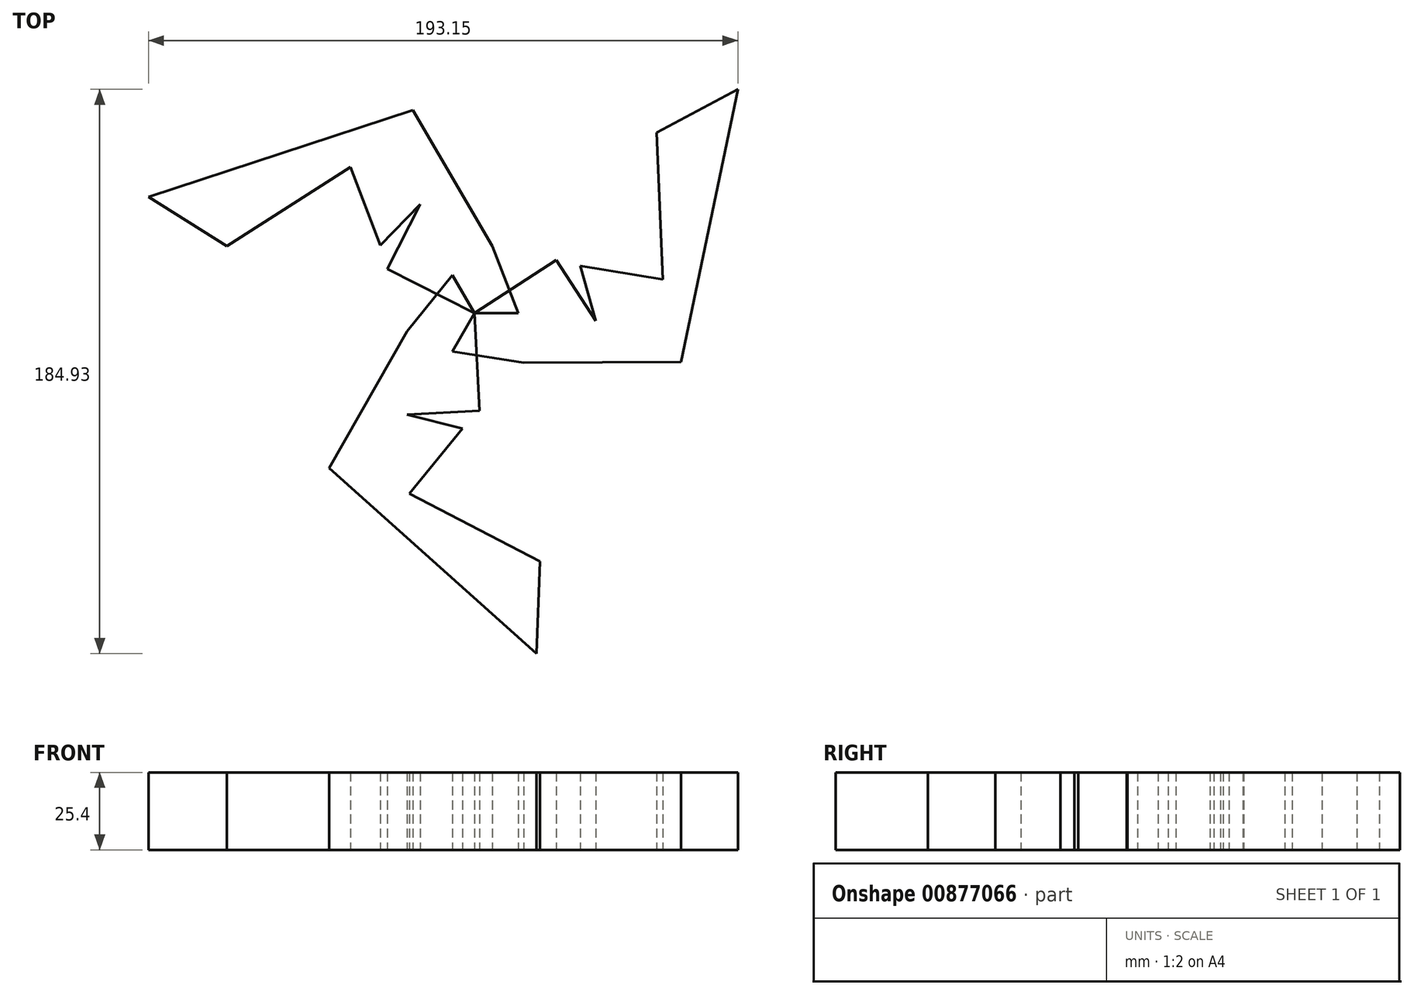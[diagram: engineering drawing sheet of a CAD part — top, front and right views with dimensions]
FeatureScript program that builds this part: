
annotation { "Feature Type Name" : "Feature", "Feature Type Description" : "" }
export const myFeature = defineFeature(function(context is Context, id is Id, definition is map)
    precondition{}
    {
        {
            var Q0;
            Q0=qCreatedBy(makeId("Top.planeOp"),FACE);
            var sketch = newSketch(context, id + "F0", { "sketchPlane" : qUnion([Q0])});
            skLineSegment(sketch, "E0", {"start": v(0, 0) * mm, "end": v(-28.53, 14.58) * mm});
            skLineSegment(sketch, "E1", {"start": v(-28.53, 14.58) * mm, "end": v(-17.72, 35.74) * mm});
            skLineSegment(sketch, "E2", {"start": v(-17.72, 35.74) * mm, "end": v(-30.77, 22.27) * mm});
            skLineSegment(sketch, "E3", {"start": v(-30.77, 22.27) * mm, "end": v(-40.57, 47.95) * mm});
            skLineSegment(sketch, "E4", {"start": v(-40.57, 47.95) * mm, "end": v(-81.18, 22.03) * mm});
            skLineSegment(sketch, "E5", {"start": v(-81.18, 22.03) * mm, "end": v(-106.77, 38.1) * mm});
            skLineSegment(sketch, "E6", {"start": v(-106.77, 38.1) * mm, "end": v(-20.11, 66.62) * mm});
            skLineSegment(sketch, "E7", {"start": v(-20.11, 66.62) * mm, "end": v(5.94, 22.03) * mm});
            skLineSegment(sketch, "E8", {"start": v(5.94, 22.03) * mm, "end": v(14.45, 0) * mm});
            skLineSegment(sketch, "E9", {"start": v(14.45, 0) * mm, "end": v(0, 0) * mm});
            skSolve(sketch);
        }
        {
            var Q0;
            Q0 = qSketchRegion(id + "F0", true);
            extrude(context, id + "F1", {"entities" : qUnion([Q0]), "depth" : 25.4 * mm, "offsetDistance" : 25.4 * mm});
        }
        {
            var Q0;
            Q0=makeQuery(id+"F1.opExtrude","SWEPT_BODY",BODY,{"disambiguationData":[OSD([sQuery(id+"F0.wireOp",EDGE,"E0"),sQuery(id+"F0.wireOp",EDGE,"E1"),sQuery(id+"F0.wireOp",EDGE,"E2"),sQuery(id+"F0.wireOp",EDGE,"E3"),sQuery(id+"F0.wireOp",EDGE,"E4"),sQuery(id+"F0.wireOp",EDGE,"E5"),sQuery(id+"F0.wireOp",EDGE,"E6"),sQuery(id+"F0.wireOp",EDGE,"E7"),sQuery(id+"F0.wireOp",EDGE,"E8"),sQuery(id+"F0.wireOp",EDGE,"E9")])]});
            var Q1;
            Q1=makeQuery(id+"F1.opExtrude","SWEPT_EDGE",EDGE,{"disambiguationData":[OSD([sQuery(id+"F0.wireOp",EDGE,"E0"),sQuery(id+"F0.wireOp",EDGE,"E9")])]});
            circularPattern(context, id + "F2", {"entities" : qUnion([Q0]), "axis" : qUnion([Q1]), "angle" : 360 * degree, "instanceCount" : 3, "equalSpace" : true});
        }
    });
